# Revit family: Floors_Floor-Construction-Pedestal_Buzon_BC-8
name_source: partatom
category: Generic Models
revit_build: Autodesk Revit 2015 (Build: 20140606_1530(x64)
units: mm (PartAtom-declared; Revit-internal decimal feet)

## types (1)
- Floors_Floor-Construction-Pedestal_Buzon_BC-8
    BIMobject category = Systems
    Brand url = http://www.buzon-world.com
    Date of publishing = 9/29/2017
    Default Elevation = 1219 mm
    Design country = Belgium
    Distance = 90 mm  [stored 0.295276 ft]
    Distance Control = 90 mm  [stored 0.295276 ft]
    Edition number = 1
    IFC Classification = Building Element
    Installation instructions = http://www.buzon-world.com
    Manufacturer = Buzon
    Manufacturer country = Belgium
    Manufacturer name = Buzon
    Material main = Polypropylene
    Material secondary = Polypropylene
    Model = BC-8
    NBS Reference Code = 20-20
    NBS Reference Description = Flooring And Decking Systems
    Nominal height = 0 mm  [stored 0 ft]
    Nominal width = 0 mm  [stored 0 ft]
    OmniClass Code = 23-15 17 11
    OmniClass Description = Flooring Specialties and Accessories
    Pedestal Material = Default_BC-8_Material
    Product Guid = 93057b95-c984-48e5-808a-a5980d588911
    Product Material = Default_BC-8_Material
    Product SKU = BC-8
    Product data url = https://bimobject.com
    Product family = BC
    Product group = Pedestal
    Product url = http://www.buzon-world.com
    QR code = http://bimobject.com
    Technical description = http://www.buzon-world.com
    UNSPSC Code = 301617
    URL = http://www.buzon-world.com
    Uniclass 1.4 Code = L83121
    Uniclass 1.4 Description = Floor units
    Uniclass 2.0 Code = SS-20-20
    Uniclass 2.0 Description = Flooring And Decking Systems
    Uniclass 2015 Code = Ss_30_42_32_30
    Uniclass 2015 Name = External floor tiling systems
    Uniformat II Code = B1010
    Uniformat II Description = Floor Construction

note: [stored X ft] marks values corroborated as IEEE doubles in the binary element streams (Revit-internal decimal feet)

## geometry (parser evidence)
native form markers: Blend x2, Sweep x56
no freeform markers — native parametric forms only
